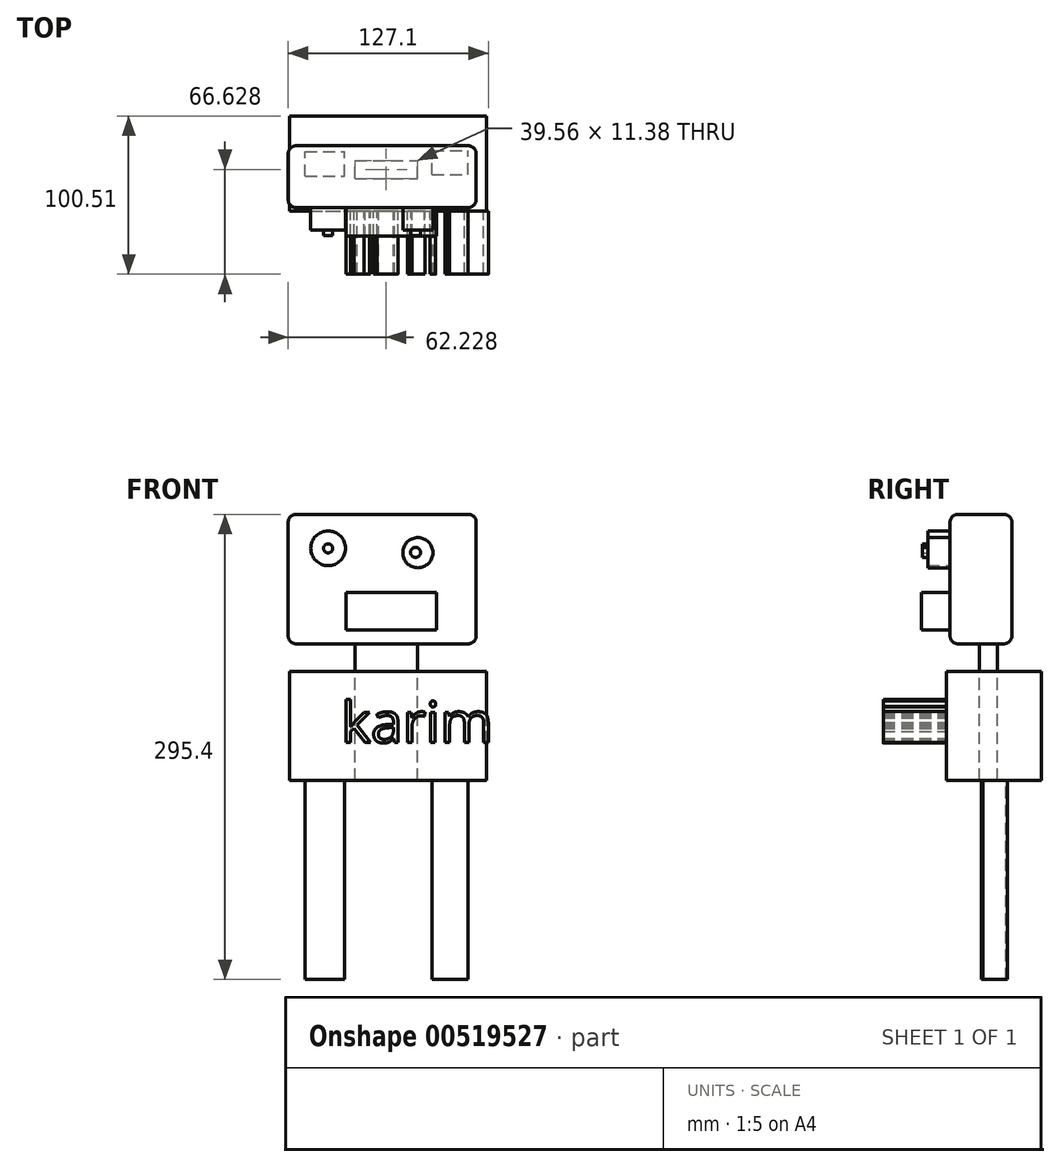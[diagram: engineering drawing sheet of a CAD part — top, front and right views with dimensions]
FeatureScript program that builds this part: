
annotation { "Feature Type Name" : "Feature", "Feature Type Description" : "" }
export const myFeature = defineFeature(function(context is Context, id is Id, definition is map)
    precondition{}
    {
        {
            var Q0;
            Q0=qCreatedBy(makeId("Front.planeOp"),FACE);
            var sketch = newSketch(context, id + "F0", { "sketchPlane" : qUnion([Q0])});
            skLineSegment(sketch, "E0.bottom", {"start": v(-105.8, 49.5) * mm, "end": v(13.57, 49.5) * mm});
            skLineSegment(sketch, "E0.top", {"start": v(-105.8, -32.7) * mm, "end": v(13.57, -32.7) * mm});
            skLineSegment(sketch, "E0.left", {"start": v(-105.8, 49.5) * mm, "end": v(-105.8, -32.7) * mm});
            skLineSegment(sketch, "E0.right", {"start": v(13.57, 49.5) * mm, "end": v(13.57, -32.7) * mm});
            skSolve(sketch);
        }
        {
            var Q0;
            Q0=makeQuery(id+"F0.imprint","IMPRINT",FACE,{"disambiguationData":[TD([[makeQuery(id+"F0.imprint","IMPRINT",EDGE,{"derivedFrom":sQuery(id+"F0.wireOp",EDGE,"E0.bottom")}),-1.0]])]});
            extrude(context, id + "F1", {"entities" : qUnion([Q0]), "depth" : 39.3 * mm, "offsetDistance" : 25 * mm});
        }
        {
            var Q0;
            Q0=makeQuery(id+"F1.opExtrude","CAP_EDGE",EDGE,{"disambiguationData":[OSD([sQuery(id+"F0.wireOp",EDGE,"E0.bottom")])],"isStart":false});
            var Q1;
            Q1=makeQuery(id+"F1.opExtrude","CAP_EDGE",EDGE,{"disambiguationData":[OSD([sQuery(id+"F0.wireOp",EDGE,"E0.left")])],"isStart":false});
            var Q2;
            Q2=makeQuery(id+"F1.opExtrude","CAP_EDGE",EDGE,{"disambiguationData":[OSD([sQuery(id+"F0.wireOp",EDGE,"E0.right")])],"isStart":false});
            var Q3;
            Q3=makeQuery(id+"F1.opExtrude","CAP_EDGE",EDGE,{"disambiguationData":[OSD([sQuery(id+"F0.wireOp",EDGE,"E0.top")])],"isStart":false});
            var Q4;
            Q4=makeQuery(id+"F1.opExtrude","CAP_EDGE",EDGE,{"disambiguationData":[OSD([sQuery(id+"F0.wireOp",EDGE,"E0.bottom")])],"isStart":true});
            var Q5;
            Q5=makeQuery(id+"F1.opExtrude","CAP_EDGE",EDGE,{"disambiguationData":[OSD([sQuery(id+"F0.wireOp",EDGE,"E0.right")])],"isStart":true});
            var Q6;
            Q6=makeQuery(id+"F1.opExtrude","CAP_EDGE",EDGE,{"disambiguationData":[OSD([sQuery(id+"F0.wireOp",EDGE,"E0.left")])],"isStart":true});
            var Q7;
            Q7=makeQuery(id+"F1.opExtrude","SWEPT_EDGE",EDGE,{"disambiguationData":[OSD([sQuery(id+"F0.wireOp",EDGE,"E0.top"),sQuery(id+"F0.wireOp",EDGE,"E0.left")])]});
            var Q8;
            Q8=makeQuery(id+"F1.opExtrude","SWEPT_EDGE",EDGE,{"disambiguationData":[OSD([sQuery(id+"F0.wireOp",EDGE,"E0.bottom"),sQuery(id+"F0.wireOp",EDGE,"E0.left")])]});
            var Q9;
            Q9=makeQuery(id+"F1.opExtrude","SWEPT_EDGE",EDGE,{"disambiguationData":[OSD([sQuery(id+"F0.wireOp",EDGE,"E0.bottom"),sQuery(id+"F0.wireOp",EDGE,"E0.right")])]});
            var Q10;
            Q10=makeQuery(id+"F1.opExtrude","SWEPT_EDGE",EDGE,{"disambiguationData":[OSD([sQuery(id+"F0.wireOp",EDGE,"E0.top"),sQuery(id+"F0.wireOp",EDGE,"E0.right")])]});
            var Q11;
            Q11=makeQuery(id+"F1.opExtrude","CAP_EDGE",EDGE,{"disambiguationData":[OSD([sQuery(id+"F0.wireOp",EDGE,"E0.top")])],"isStart":true});
            fillet(context, id + "F2", {"entities" : qUnion([Q0, Q1, Q2, Q3, Q4, Q5, Q6, Q7, Q8, Q9, Q10, Q11]), "radius" : 5 * mm, "tangentPropagation" : true, "allowEdgeOverflow" : false});
        }
        {
            var Q0;
            Q0=makeQuery(id+"F1.opExtrude","CAP_FACE",FACE,{"disambiguationData":[OSD([sQuery(id+"F0.wireOp",EDGE,"E0.bottom"),sQuery(id+"F0.wireOp",EDGE,"E0.top"),sQuery(id+"F0.wireOp",EDGE,"E0.left"),sQuery(id+"F0.wireOp",EDGE,"E0.right")])],"isStart":false});
            var sketch = newSketch(context, id + "F3", { "sketchPlane" : qUnion([Q0])});
            skCircle(sketch, "E1", {"center": v(-80.44, 27.94) * mm, "radius": 11.05 * mm});
            skCircle(sketch, "E2", {"center": v(-23.45, 25.13) * mm, "radius": 9.57 * mm});
            skSolve(sketch);
        }
        {
            var Q0;
            Q0=makeQuery(id+"F3.imprint","IMPRINT",FACE,{"disambiguationData":[TD([[makeQuery(id+"F3.imprint","IMPRINT",EDGE,{"derivedFrom":sQuery(id+"F3.wireOp",EDGE,"E2")}),1.0]])]});
            var Q1;
            Q1=makeQuery(id+"F3.imprint","IMPRINT",FACE,{"disambiguationData":[TD([[makeQuery(id+"F3.imprint","IMPRINT",EDGE,{"derivedFrom":sQuery(id+"F3.wireOp",EDGE,"E1")}),1.0]])]});
            extrude(context, id + "F4", {"entities" : qUnion([Q0, Q1]), "operationType" : NewBodyOperationType.ADD, "depth" : 14.2 * mm, "offsetDistance" : 25 * mm});
        }
        {
            var Q0;
            Q0=makeQuery(id+"F4.opExtrude","CAP_FACE",FACE,{"disambiguationData":[OSD([sQuery(id+"F3.wireOp",EDGE,"E1")])],"isStart":false});
            var sketch = newSketch(context, id + "F5", { "sketchPlane" : qUnion([Q0])});
            skCircle(sketch, "E3", {"center": v(-80.44, 27.94) * mm, "radius": 2.9 * mm});
            skCircle(sketch, "E4", {"center": v(-24.92, 25.38) * mm, "radius": 3.22 * mm});
            skSolve(sketch);
        }
        {
            var Q0;
            Q0=makeQuery(id+"F5.imprint","IMPRINT",FACE,{"disambiguationData":[TD([[makeQuery(id+"F5.imprint","IMPRINT",EDGE,{"derivedFrom":sQuery(id+"F5.wireOp",EDGE,"E3")}),1.0]])]});
            var Q1;
            Q1=makeQuery(id+"F5.imprint","IMPRINT",FACE,{"disambiguationData":[TD([[makeQuery(id+"F5.imprint","IMPRINT",EDGE,{"derivedFrom":sQuery(id+"F5.wireOp",EDGE,"E4")}),1.0]])]});
            extrude(context, id + "F6", {"entities" : qUnion([Q0, Q1]), "operationType" : NewBodyOperationType.ADD, "depth" : 3.5 * mm, "offsetDistance" : 25 * mm});
        }
        {
            var Q0;
            Q0=makeQuery(id+"F1.opExtrude","CAP_FACE",FACE,{"disambiguationData":[OSD([sQuery(id+"F0.wireOp",EDGE,"E0.bottom"),sQuery(id+"F0.wireOp",EDGE,"E0.top"),sQuery(id+"F0.wireOp",EDGE,"E0.left"),sQuery(id+"F0.wireOp",EDGE,"E0.right")])],"isStart":false});
            var sketch = newSketch(context, id + "F7", { "sketchPlane" : qUnion([Q0])});
            skLineSegment(sketch, "E5.bottom", {"start": v(-69.15, 0) * mm, "end": v(-11.67, 0) * mm});
            skLineSegment(sketch, "E5.top", {"start": v(-69.15, -23.89) * mm, "end": v(-11.67, -23.89) * mm});
            skLineSegment(sketch, "E5.left", {"start": v(-69.15, 0) * mm, "end": v(-69.15, -23.89) * mm});
            skLineSegment(sketch, "E5.right", {"start": v(-11.67, 0) * mm, "end": v(-11.67, -23.89) * mm});
            skSolve(sketch);
        }
        {
            var Q0;
            Q0=makeQuery(id+"F7.imprint","IMPRINT",FACE,{"disambiguationData":[TD([[makeQuery(id+"F7.imprint","IMPRINT",EDGE,{"derivedFrom":sQuery(id+"F7.wireOp",EDGE,"E5.bottom")}),-1.0]])]});
            extrude(context, id + "F8", {"entities" : qUnion([Q0]), "operationType" : NewBodyOperationType.ADD, "depth" : 18.1 * mm, "offsetDistance" : 25 * mm});
        }
        {
            var Q0;
            Q0=makeQuery(id+"F1.opExtrude","SWEPT_FACE",FACE,{"disambiguationData":[OSD([sQuery(id+"F0.wireOp",EDGE,"E0.top")])]});
            var sketch = newSketch(context, id + "F9", { "sketchPlane" : qUnion([Q0])});
            skLineSegment(sketch, "E6.bottom", {"start": v(-63.36, 20.71) * mm, "end": v(-23.8, 20.71) * mm});
            skLineSegment(sketch, "E6.top", {"start": v(-63.36, 9.33) * mm, "end": v(-23.8, 9.33) * mm});
            skLineSegment(sketch, "E6.left", {"start": v(-63.36, 20.71) * mm, "end": v(-63.36, 9.33) * mm});
            skLineSegment(sketch, "E6.right", {"start": v(-23.8, 20.71) * mm, "end": v(-23.8, 9.33) * mm});
            skSolve(sketch);
        }
        {
            var Q0;
            Q0=makeQuery(id+"F9.imprint","IMPRINT",FACE,{"disambiguationData":[TD([[makeQuery(id+"F9.imprint","IMPRINT",EDGE,{"derivedFrom":sQuery(id+"F9.wireOp",EDGE,"E6.bottom")}),-1.0]])]});
            extrude(context, id + "F10", {"entities" : qUnion([Q0]), "operationType" : NewBodyOperationType.ADD, "depth" : 17.6 * mm, "offsetDistance" : 25 * mm});
        }
        {
            var Q0;
            Q0=makeQuery(id+"F10.opExtrude","CAP_FACE",FACE,{"disambiguationData":[OSD([sQuery(id+"F9.wireOp",EDGE,"E6.bottom"),sQuery(id+"F9.wireOp",EDGE,"E6.top"),sQuery(id+"F9.wireOp",EDGE,"E6.left"),sQuery(id+"F9.wireOp",EDGE,"E6.right")])],"isStart":false});
            var sketch = newSketch(context, id + "F11", { "sketchPlane" : qUnion([Q0])});
            skLineSegment(sketch, "E7.bottom", {"start": v(-105.07, 41.65) * mm, "end": v(20.14, 41.65) * mm});
            skLineSegment(sketch, "E7.top", {"start": v(-105.07, -18.86) * mm, "end": v(20.14, -18.86) * mm});
            skLineSegment(sketch, "E7.left", {"start": v(-105.07, 41.65) * mm, "end": v(-105.07, -18.86) * mm});
            skLineSegment(sketch, "E7.right", {"start": v(20.14, 41.65) * mm, "end": v(20.14, -18.86) * mm});
            skSolve(sketch);
        }
        {
            var Q0;
            Q0=makeQuery(id+"F11.imprint","IMPRINT",FACE,{"disambiguationData":[TD([[makeQuery(id+"F11.imprint","IMPRINT",EDGE,{"derivedFrom":sQuery(id+"F11.wireOp",EDGE,"E7.bottom")}),-1.0]])]});
            extrude(context, id + "F12", {"entities" : qUnion([Q0]), "depth" : 69.1 * mm, "offsetDistance" : 25 * mm});
        }
        {
            var Q0;
            Q0=makeQuery(id+"F12.opExtrude","CAP_FACE",FACE,{"disambiguationData":[OSD([sQuery(id+"F9.wireOp",EDGE,"E6.bottom"),sQuery(id+"F9.wireOp",EDGE,"E6.top"),sQuery(id+"F9.wireOp",EDGE,"E6.left"),sQuery(id+"F9.wireOp",EDGE,"E6.right"),sQuery(id+"F11.wireOp",EDGE,"E7.bottom"),sQuery(id+"F11.wireOp",EDGE,"E7.top"),sQuery(id+"F11.wireOp",EDGE,"E7.left"),sQuery(id+"F11.wireOp",EDGE,"E7.right")])],"isStart":false});
            var sketch = newSketch(context, id + "F13", { "sketchPlane" : qUnion([Q0])});
            skLineSegment(sketch, "E8.bottom", {"start": v(-95.09, 19.4) * mm, "end": v(-69.9, 19.4) * mm});
            skLineSegment(sketch, "E8.top", {"start": v(-95.09, 3.73) * mm, "end": v(-69.9, 3.73) * mm});
            skLineSegment(sketch, "E8.left", {"start": v(-95.09, 19.4) * mm, "end": v(-95.09, 3.73) * mm});
            skLineSegment(sketch, "E8.right", {"start": v(-69.9, 19.4) * mm, "end": v(-69.9, 3.73) * mm});
            skLineSegment(sketch, "E9.bottom", {"start": v(-14.47, 18.47) * mm, "end": v(8.3, 18.47) * mm});
            skLineSegment(sketch, "E9.top", {"start": v(-14.47, 2.99) * mm, "end": v(8.3, 2.99) * mm});
            skLineSegment(sketch, "E9.left", {"start": v(-14.47, 18.47) * mm, "end": v(-14.47, 2.99) * mm});
            skLineSegment(sketch, "E9.right", {"start": v(8.3, 18.47) * mm, "end": v(8.3, 2.99) * mm});
            skLineSegment(sketch, "E10.bottom", {"start": v(8.3, 2.99) * mm, "end": v(-11.11, 2.99) * mm});
            skLineSegment(sketch, "E10.top", {"start": v(8.3, 2.99) * mm, "end": v(-11.11, 2.99) * mm});
            skLineSegment(sketch, "E10.left", {"start": v(8.3, 2.99) * mm, "end": v(8.3, 2.99) * mm});
            skLineSegment(sketch, "E10.right", {"start": v(-11.11, 2.99) * mm, "end": v(-11.11, 2.99) * mm});
            skSolve(sketch);
        }
        {
            var Q0;
            Q0=makeQuery(id+"F13.imprint","IMPRINT",FACE,{"disambiguationData":[TD([[makeQuery(id+"F13.imprint","IMPRINT",EDGE,{"derivedFrom":sQuery(id+"F13.wireOp",EDGE,"E8.bottom")}),-1.0]])]});
            var Q1;
            Q1=makeQuery(id+"F13.imprint","IMPRINT",FACE,{"disambiguationData":[TD([[makeQuery(id+"F13.imprint","IMPRINT",EDGE,{"derivedFrom":sQuery(id+"F13.wireOp",EDGE,"E9.bottom")}),-1.0]])]});
            extrude(context, id + "F14", {"entities" : qUnion([Q0, Q1]), "operationType" : NewBodyOperationType.ADD, "depth" : 126.5 * mm, "offsetDistance" : 25 * mm});
        }
        {
            var Q0;
            Q0=makeQuery(id+"F12.opExtrude","SWEPT_FACE",FACE,{"disambiguationData":[OSD([sQuery(id+"F11.wireOp",EDGE,"E7.bottom")])]});
            var sketch = newSketch(context, id + "F15", { "sketchPlane" : qUnion([Q0])});
            skText(sketch, "E11", { "text": "karim", "fontName": "OpenSans-Regular.ttf"});
            const initialGuessF15  = {"E11": [-0.0721, -0.09544, 1, 0, 0.02595]};
            skSetInitialGuess(sketch, initialGuessF15);
            skSolve(sketch);
        }
        {
            var Q0;
            Q0 = qSketchRegion(id + "F15", true);
            extrude(context, id + "F16", {"entities" : qUnion([Q0]), "operationType" : NewBodyOperationType.ADD, "depth" : 40 * mm, "offsetDistance" : 25 * mm});
        }
    });
